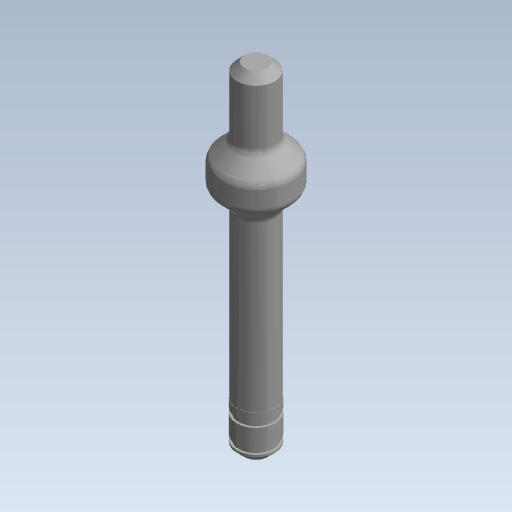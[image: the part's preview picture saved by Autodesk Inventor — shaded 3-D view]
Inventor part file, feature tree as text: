
AUTODESK INVENTOR PART (.ipt)
format: ipt  version: 2020 (Build 240168000, 168)  size: 99,328 bytes
history: native  units: mm (DEFAULTED — no unit token found)
features: chamfer x1
ambient origin geometry x8: Origin, YZ Plane, XZ Plane, XY Plane, X Axis, Y Axis, Z Axis, Center Point
bodies: Solid1 (feature_tree)
feature tree (1):
  chamfer  "Chamfer1"  [1 undecoded]
note: 1 required parameter value undecoded (feature->parameter linkage not recoverable at this tier; creation-order binding heuristic only, values carry confidence <= 0.55)
